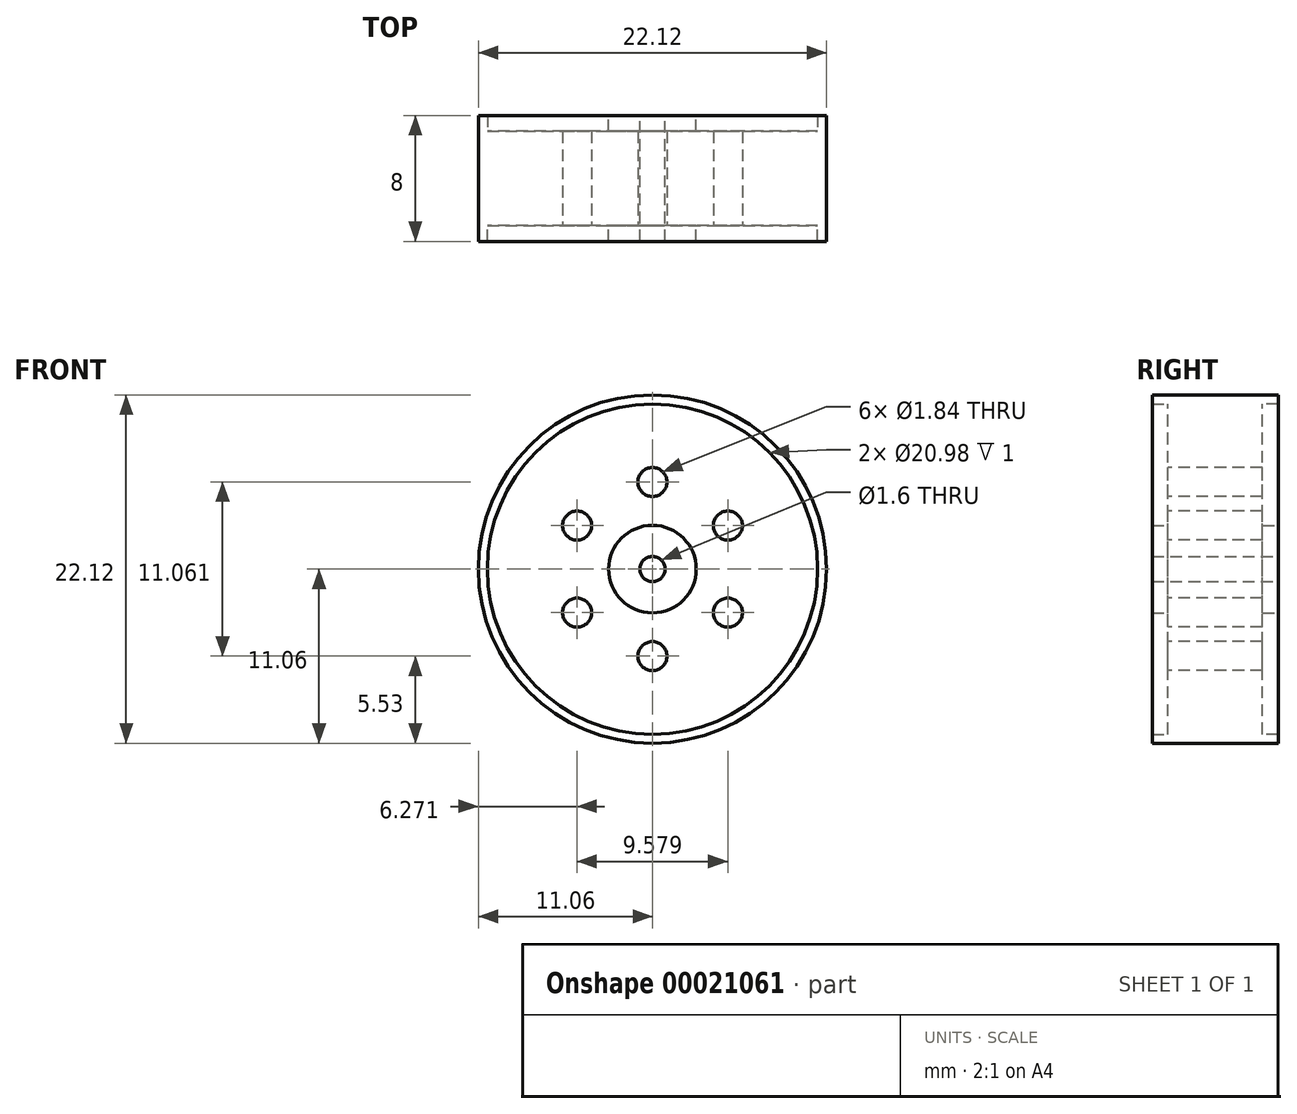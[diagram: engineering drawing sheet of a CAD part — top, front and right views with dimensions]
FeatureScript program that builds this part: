
annotation { "Feature Type Name" : "Feature", "Feature Type Description" : "" }
export const myFeature = defineFeature(function(context is Context, id is Id, definition is map)
    precondition{}
    {
        {
            var Q0;
            Q0=qCreatedBy(makeId("Front.planeOp"),FACE);
            var sketch = newSketch(context, id + "F0", { "sketchPlane" : qUnion([Q0])});
            skCircle(sketch, "E0", {"center": v(0, 0) * mm, "radius": 11.06 * mm});
            skCircle(sketch, "E1", {"center": v(0, 0) * mm, "radius": 0.8 * mm});
            skCircle(sketch, "E2", {"center": v(0, 5.53) * mm, "radius": 0.92 * mm});
            skCircle(sketch, "E3", {"center": v(4.79, 2.77) * mm, "radius": 0.92 * mm});
            skCircle(sketch, "E4", {"center": v(4.79, -2.77) * mm, "radius": 0.92 * mm});
            skCircle(sketch, "E5", {"center": v(0, -5.53) * mm, "radius": 0.92 * mm});
            skCircle(sketch, "E6", {"center": v(-4.79, -2.77) * mm, "radius": 0.92 * mm});
            skCircle(sketch, "E7", {"center": v(-4.79, 2.77) * mm, "radius": 0.92 * mm});
            skLineSegment(sketch, "E8", {"start": v(0, 5.53) * mm, "end": v(0, 4.6) * mm});
            skLineSegment(sketch, "E9.trimOffspring", {"start": v(0, -4.6) * mm, "end": v(0, -5.53) * mm});
            skCircle(sketch, "E10", {"center": v(0, 0) * mm, "radius": 2.78 * mm});
            skCircle(sketch, "E11", {"center": v(0, 0) * mm, "radius": 10.49 * mm});
            skSolve(sketch);
        }
        {
            var Q0;
            Q0=makeQuery(id+"F0.imprint","IMPRINT",FACE,{"disambiguationData":[TD([[makeQuery(id+"F0.imprint","IMPRINT",EDGE,{"derivedFrom":sQuery(id+"F0.wireOp",EDGE,"E0")}),1.0]])]});
            extrude(context, id + "F1", {"entities" : qUnion([Q0]), "oppositeDirection" : true, "depth" : 6 * mm});
        }
        {
            var Q0;
            Q0=makeQuery(id+"F0.imprint","IMPRINT",FACE,{"disambiguationData":[TD([[makeQuery(id+"F0.imprint","IMPRINT",EDGE,{"derivedFrom":sQuery(id+"F0.wireOp",EDGE,"E10")}),1.0]])]});
            extrude(context, id + "F2", {"entities" : qUnion([Q0]), "depth" : 1 * mm});
        }
        {
            var Q0;
            Q0=makeQuery(id+"F2.opExtrude","CAP_FACE",FACE,{"disambiguationData":[OSD([sQuery(id+"F0.wireOp",EDGE,"E1"),sQuery(id+"F0.wireOp",EDGE,"E10")])],"isStart":false});
            extrude(context, id + "F3", {"entities" : qUnion([Q0]), "oppositeDirection" : true, "depth" : 6 * mm});
        }
        {
            var Q0;
            Q0=makeQuery(id+"F0.imprint","IMPRINT",FACE,{"disambiguationData":[TD([[makeQuery(id+"F0.imprint","IMPRINT",EDGE,{"derivedFrom":sQuery(id+"F0.wireOp",EDGE,"E2")}),-1.0]])]});
            extrude(context, id + "F4", {"entities" : qUnion([Q0]), "oppositeDirection" : true, "depth" : 6 * mm});
        }
        {
            var Q0;
            Q0=makeQuery(id+"F1.opExtrude","CAP_FACE",FACE,{"disambiguationData":[OSD([sQuery(id+"F0.wireOp",EDGE,"E0"),sQuery(id+"F0.wireOp",EDGE,"E11")])],"isStart":false});
            extrude(context, id + "F5", {"entities" : qUnion([Q0]), "operationType" : NewBodyOperationType.ADD, "oppositeDirection" : true, "depth" : 7 * mm});
        }
        {
            var Q0;
            Q0=makeQuery(id+"F5.opExtrude","CAP_FACE",FACE,{"disambiguationData":[OSD([sQuery(id+"F0.wireOp",EDGE,"E0"),sQuery(id+"F0.wireOp",EDGE,"E11")])],"isStart":false});
            extrude(context, id + "F6", {"entities" : qUnion([Q0]), "operationType" : NewBodyOperationType.ADD, "oppositeDirection" : true, "depth" : 8 * mm});
        }
        {
            var Q0;
            Q0=makeQuery(id+"F2.opExtrude","CAP_FACE",FACE,{"disambiguationData":[OSD([sQuery(id+"F0.wireOp",EDGE,"E1"),sQuery(id+"F0.wireOp",EDGE,"E10")])],"isStart":false});
            extrude(context, id + "F7", {"entities" : qUnion([Q0]), "operationType" : NewBodyOperationType.ADD, "oppositeDirection" : true, "depth" : 8 * mm});
        }
    });
